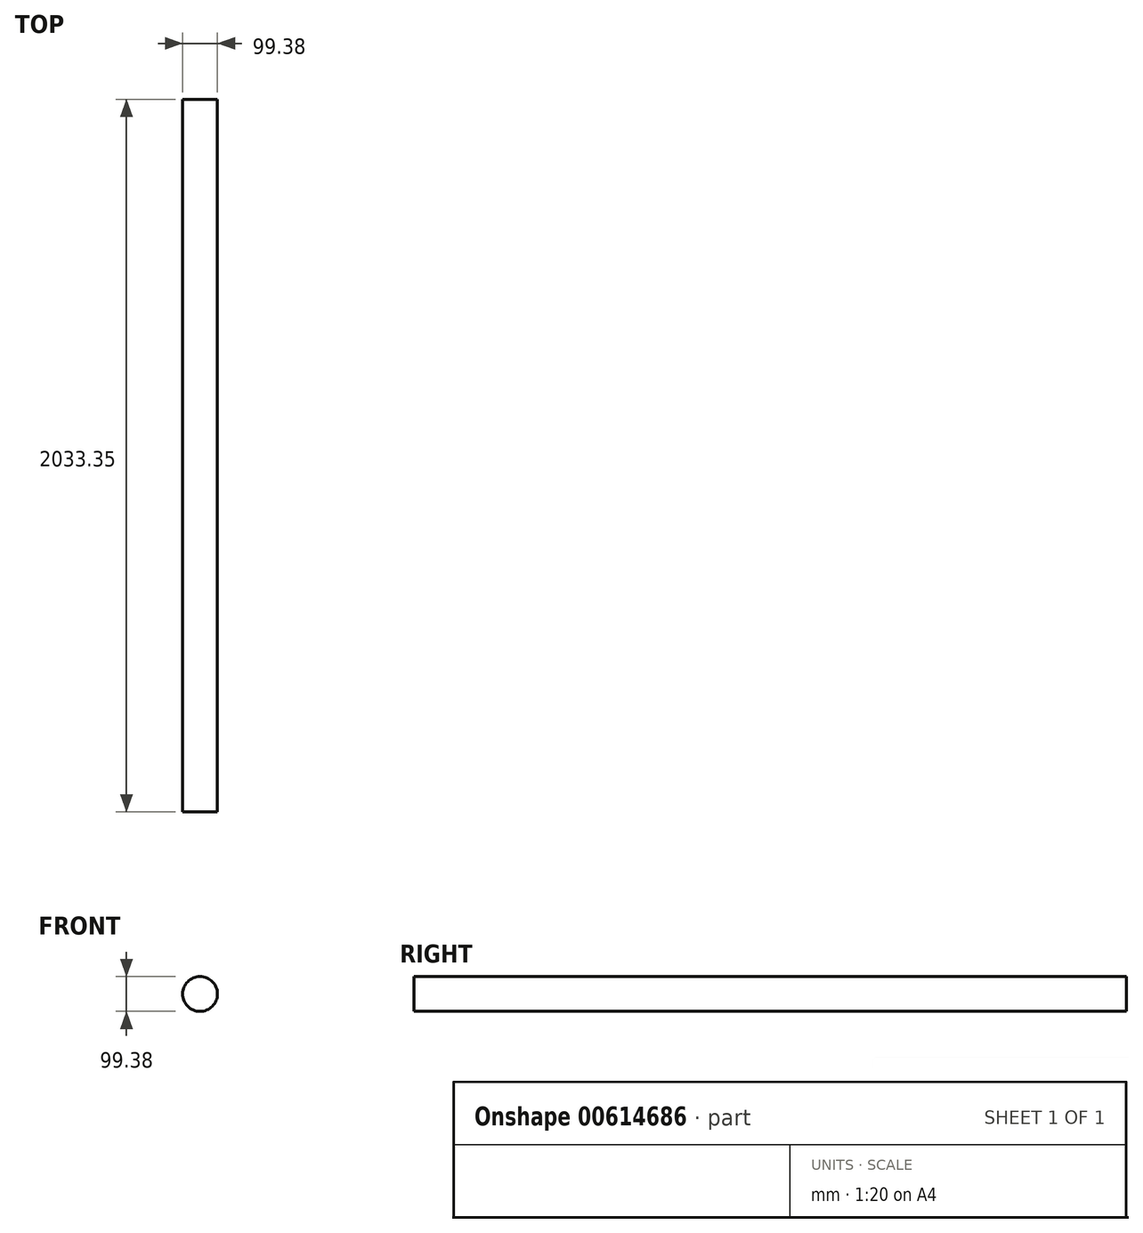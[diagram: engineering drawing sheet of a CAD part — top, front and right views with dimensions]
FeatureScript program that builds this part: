
annotation { "Feature Type Name" : "Feature", "Feature Type Description" : "" }
export const myFeature = defineFeature(function(context is Context, id is Id, definition is map)
    precondition{}
    {
        {
            var Q0;
            Q0=qCreatedBy(makeId("Front.planeOp"),FACE);
            var sketch = newSketch(context, id + "F0", { "sketchPlane" : qUnion([Q0])});
            skCircle(sketch, "E0", {"center": v(0, 0) * mm, "radius": 49.7 * mm});
            skSolve(sketch);
        }
        {
            var Q0;
            Q0=makeQuery(id+"F0.imprint","IMPRINT",FACE,{"disambiguationData":[TD([[makeQuery(id+"F0.imprint","IMPRINT",EDGE,{"derivedFrom":sQuery(id+"F0.wireOp",EDGE,"E0")}),1.0]])]});
            extrude(context, id + "F1", {"entities" : qUnion([Q0]), "depth" : 2033.35 * mm, "offsetDistance" : 25.4 * mm});
        }
    });
